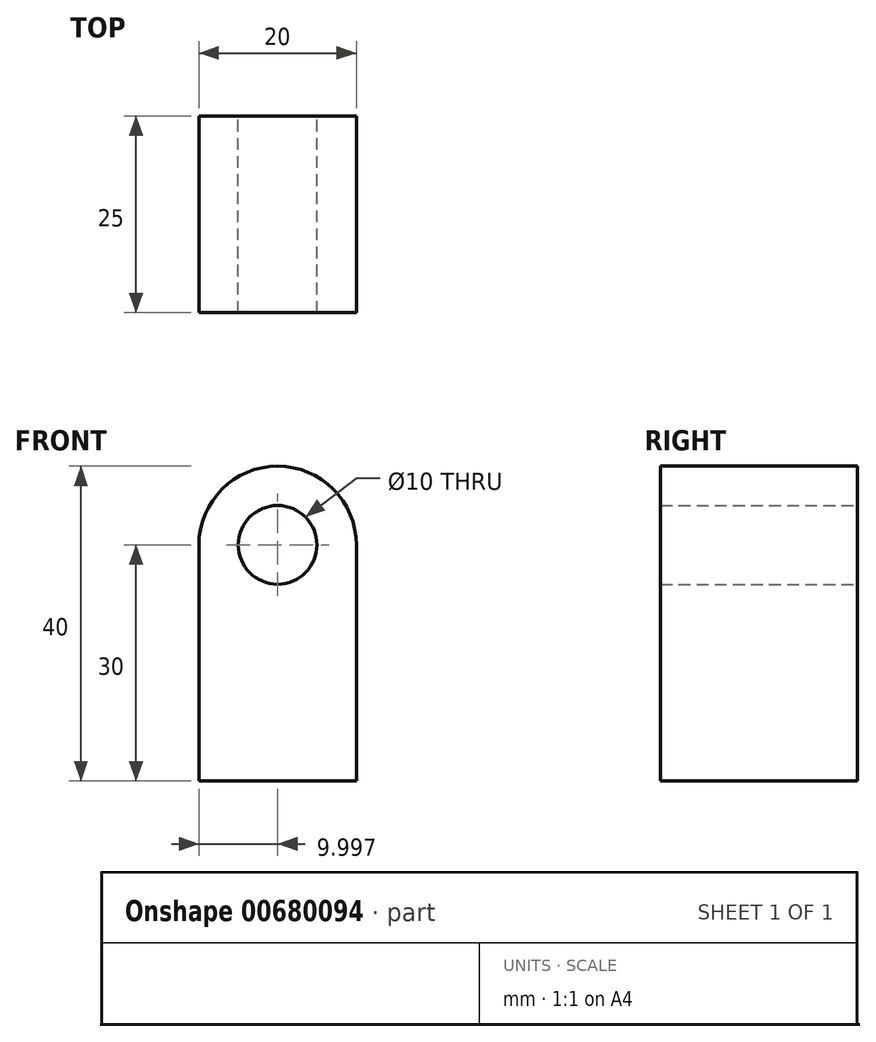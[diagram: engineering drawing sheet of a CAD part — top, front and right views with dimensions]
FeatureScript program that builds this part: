
annotation { "Feature Type Name" : "Feature", "Feature Type Description" : "" }
export const myFeature = defineFeature(function(context is Context, id is Id, definition is map)
    precondition{}
    {
        {
            var Q0;
            Q0=qCreatedBy(makeId("Front.planeOp"),FACE);
            var sketch = newSketch(context, id + "F0", { "sketchPlane" : qUnion([Q0])});
            skLineSegment(sketch, "E0.bottom", {"start": v(-36.11, 0) * mm, "end": v(-16.11, 0) * mm});
            skLineSegment(sketch, "E0.left", {"start": v(-36.11, 0) * mm, "end": v(-36.11, 30) * mm});
            skLineSegment(sketch, "E0.right", {"start": v(-16.11, 0) * mm, "end": v(-16.11, 30) * mm});
            skArc(sketch, "E1", {"start": v(-16.11, 30) * mm, "mid": v(-26.11, 40) * mm, "end": v(-36.11, 30) * mm});
            skCircle(sketch, "E2", {"center": v(-26.11, 30) * mm, "radius": 5 * mm});
            skSolve(sketch);
        }
        {
            var Q0;
            Q0 = qSketchRegion(id + "F0", true);
            extrude(context, id + "F1", {"entities" : qUnion([Q0]), "depth" : 25 * mm, "offsetDistance" : 25 * mm});
        }
    });
